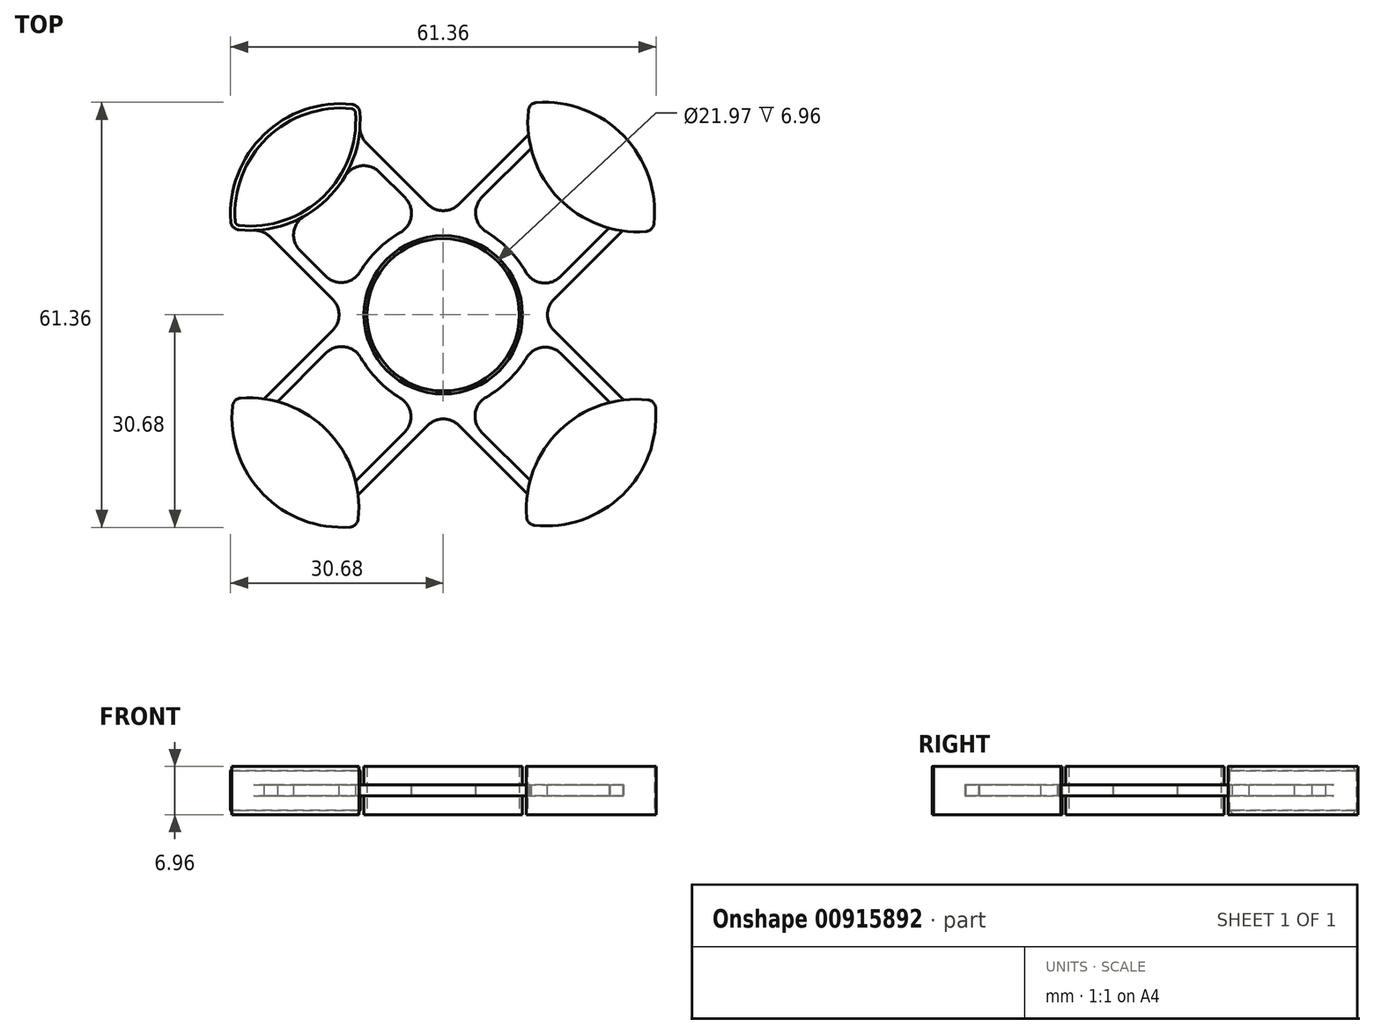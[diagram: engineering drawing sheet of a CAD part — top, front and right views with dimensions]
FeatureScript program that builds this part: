
annotation { "Feature Type Name" : "Feature", "Feature Type Description" : "" }
export const myFeature = defineFeature(function(context is Context, id is Id, definition is map)
    precondition{}
    {
        {
            var Q0;
            Q0=qCreatedBy(makeId("Top.planeOp"),FACE);
            var sketch = newSketch(context, id + "F0", { "sketchPlane" : qUnion([Q0])});
            skCircle(sketch, "E0", {"center": v(0, 0) * mm, "radius": 11.43 * mm});
            skLineSegment(sketch, "E1", {"start": v(-28.3, 14.58) * mm, "end": v(-14.37, 28.08) * mm});
            skLineSegment(sketch, "E2.MirrorCS", {"start": v(-14.37, 28.08) * mm, "end": v(0, 13.72) * mm});
            skLineSegment(sketch, "E3.MirrorCS", {"start": v(-13.72, 0) * mm, "end": v(-28.3, 14.58) * mm});
            skLineSegment(sketch, "E4", {"start": v(-13.73, 2.35) * mm, "end": v(-24.41, 13.03) * mm});
            skLineSegment(sketch, "E5", {"start": v(-12.86, 24.24) * mm, "end": v(-2.17, 13.55) * mm});
            skArc(sketch, "E6", {"start": v(-2.17, 13.55) * mm, "mid": v(-9.4, 9.45) * mm, "end": v(-13.73, 2.35) * mm});
            skArc(sketch, "E7", {"start": v(-12.86, 24.24) * mm, "mid": v(-20.1, 20.14) * mm, "end": v(-24.41, 13.03) * mm});
            skArc(sketch, "E8.1.0", {"start": v(-24.24, -12.86) * mm, "mid": v(-20.14, -20.1) * mm, "end": v(-13.03, -24.41) * mm});
            skArc(sketch, "E8.1.1", {"start": v(-13.55, -2.17) * mm, "mid": v(-9.45, -9.4) * mm, "end": v(-2.35, -13.73) * mm});
            skLineSegment(sketch, "E8.1.2", {"start": v(-14.58, -28.3) * mm, "end": v(-28.08, -14.37) * mm});
            skLineSegment(sketch, "E8.1.3", {"start": v(-24.24, -12.86) * mm, "end": v(-13.55, -2.17) * mm});
            skLineSegment(sketch, "E8.1.4", {"start": v(0, -13.72) * mm, "end": v(-14.58, -28.3) * mm});
            skLineSegment(sketch, "E8.1.5", {"start": v(-2.35, -13.73) * mm, "end": v(-13.03, -24.41) * mm});
            skLineSegment(sketch, "E8.1.6", {"start": v(-28.08, -14.37) * mm, "end": v(-13.72, 0) * mm});
            skArc(sketch, "E8.2.0", {"start": v(12.86, -24.24) * mm, "mid": v(20.1, -20.14) * mm, "end": v(24.41, -13.03) * mm});
            skArc(sketch, "E8.2.1", {"start": v(2.17, -13.55) * mm, "mid": v(9.4, -9.45) * mm, "end": v(13.73, -2.35) * mm});
            skLineSegment(sketch, "E8.2.2", {"start": v(28.3, -14.58) * mm, "end": v(14.37, -28.08) * mm});
            skLineSegment(sketch, "E8.2.3", {"start": v(12.86, -24.24) * mm, "end": v(2.17, -13.55) * mm});
            skLineSegment(sketch, "E8.2.4", {"start": v(13.72, 0) * mm, "end": v(28.3, -14.58) * mm});
            skLineSegment(sketch, "E8.2.5", {"start": v(13.73, -2.35) * mm, "end": v(24.41, -13.03) * mm});
            skLineSegment(sketch, "E8.2.6", {"start": v(14.37, -28.08) * mm, "end": v(0, -13.72) * mm});
            skArc(sketch, "E8.3.0", {"start": v(24.24, 12.86) * mm, "mid": v(20.14, 20.1) * mm, "end": v(13.03, 24.41) * mm});
            skArc(sketch, "E8.3.1", {"start": v(13.55, 2.17) * mm, "mid": v(9.45, 9.4) * mm, "end": v(2.35, 13.73) * mm});
            skLineSegment(sketch, "E8.3.2", {"start": v(14.58, 28.3) * mm, "end": v(28.08, 14.37) * mm});
            skLineSegment(sketch, "E8.3.3", {"start": v(24.24, 12.86) * mm, "end": v(13.55, 2.17) * mm});
            skLineSegment(sketch, "E8.3.4", {"start": v(0, 13.72) * mm, "end": v(14.58, 28.3) * mm});
            skLineSegment(sketch, "E8.3.5", {"start": v(2.35, 13.73) * mm, "end": v(13.03, 24.41) * mm});
            skLineSegment(sketch, "E8.3.6", {"start": v(28.08, 14.37) * mm, "end": v(13.72, 0) * mm});
            skSolve(sketch);
        }
        {
            var Q0;
            Q0=qSketchRegion(id+"F0",true);
            extrude(context, id + "F1", {"entities" : qUnion([Q0]), "endBound" : BoundingType.SYMMETRIC, "depth" : 1.59 * mm, "offsetDistance" : 25.4 * mm});
        }
        {
            var Q0;
            Q0=qCreatedBy(makeId("Top.planeOp"),FACE);
            var sketch = newSketch(context, id + "F2", { "sketchPlane" : qUnion([Q0])});
            skCircle(sketch, "E9", {"center": v(0, 0) * mm, "radius": 10.99 * mm});
            skCircle(sketch, "E10", {"center": v(0, 0) * mm, "radius": 11.43 * mm});
            skSolve(sketch);
        }
        {
            var Q0;
            Q0=qSketchRegion(id+"F2",true);
            extrude(context, id + "F3", {"entities" : qUnion([Q0]), "operationType" : NewBodyOperationType.ADD, "endBound" : BoundingType.SYMMETRIC, "depth" : 6.96 * mm, "offsetDistance" : 25.4 * mm});
        }
        {
            var Q0;
            Q0=qCreatedBy(makeId("Top.planeOp"),FACE);
            var sketch = newSketch(context, id + "F4", { "sketchPlane" : qUnion([Q0])});
            skArc(sketch, "E11.1.0", {"start": v(-30.64, 13.44) * mm, "mid": v(-25.86, 26) * mm, "end": v(-13.16, 30.4) * mm});
            skPoint(sketch, "E11.1.1", {"position": v(-30.53, 12.4) * mm});
            skArc(sketch, "E11.1.2", {"start": v(-29.5, 12.27) * mm, "mid": v(-16.8, 16.66) * mm, "end": v(-12.03, 29.22) * mm});
            skLineSegment(sketch, "E11.1.3", {"start": v(-30.53, 12.4) * mm, "end": v(-12.13, 30.25) * mm});
            skPoint(sketch, "E11.1.4", {"position": v(-12.13, 30.25) * mm});
            skPoint(sketch, "E11.1.5", {"position": v(-30.53, 12.4) * mm});
            skArc(sketch, "E11.1.6", {"start": v(-12.03, 29.22) * mm, "mid": v(-12.38, 30.01) * mm, "end": v(-13.16, 30.4) * mm});
            skArc(sketch, "E11.1.7", {"start": v(-30.64, 13.44) * mm, "mid": v(-30.28, 12.65) * mm, "end": v(-29.5, 12.27) * mm});
            skPoint(sketch, "E11.center", {"position": v(0, 0) * mm});
            skArc(sketch, "E12.1.0", {"start": v(-13.44, -30.64) * mm, "mid": v(-26, -25.86) * mm, "end": v(-30.4, -13.16) * mm});
            skPoint(sketch, "E12.1.1", {"position": v(-12.4, -30.53) * mm});
            skLineSegment(sketch, "E12.1.2", {"start": v(-12.4, -30.53) * mm, "end": v(-30.25, -12.13) * mm});
            skPoint(sketch, "E12.1.3", {"position": v(-30.25, -12.13) * mm});
            skArc(sketch, "E12.1.4", {"start": v(-12.27, -29.5) * mm, "mid": v(-16.66, -16.8) * mm, "end": v(-29.22, -12.03) * mm});
            skPoint(sketch, "E12.1.5", {"position": v(-12.4, -30.53) * mm});
            skArc(sketch, "E12.1.6", {"start": v(-13.44, -30.64) * mm, "mid": v(-12.65, -30.28) * mm, "end": v(-12.27, -29.5) * mm});
            skArc(sketch, "E12.1.7", {"start": v(-29.22, -12.03) * mm, "mid": v(-30.01, -12.38) * mm, "end": v(-30.4, -13.16) * mm});
            skArc(sketch, "E12.2.0", {"start": v(30.64, -13.44) * mm, "mid": v(25.86, -26) * mm, "end": v(13.16, -30.4) * mm});
            skPoint(sketch, "E12.2.1", {"position": v(30.53, -12.4) * mm});
            skLineSegment(sketch, "E12.2.2", {"start": v(30.53, -12.4) * mm, "end": v(12.13, -30.25) * mm});
            skPoint(sketch, "E12.2.3", {"position": v(12.13, -30.25) * mm});
            skArc(sketch, "E12.2.4", {"start": v(29.5, -12.27) * mm, "mid": v(16.8, -16.66) * mm, "end": v(12.03, -29.22) * mm});
            skPoint(sketch, "E12.2.5", {"position": v(30.53, -12.4) * mm});
            skArc(sketch, "E12.2.6", {"start": v(30.64, -13.44) * mm, "mid": v(30.28, -12.65) * mm, "end": v(29.5, -12.27) * mm});
            skArc(sketch, "E12.2.7", {"start": v(12.03, -29.22) * mm, "mid": v(12.38, -30.01) * mm, "end": v(13.16, -30.4) * mm});
            skArc(sketch, "E12.3.0", {"start": v(13.44, 30.64) * mm, "mid": v(26, 25.86) * mm, "end": v(30.4, 13.16) * mm});
            skPoint(sketch, "E12.3.1", {"position": v(12.4, 30.53) * mm});
            skLineSegment(sketch, "E12.3.2", {"start": v(12.4, 30.53) * mm, "end": v(30.25, 12.13) * mm});
            skPoint(sketch, "E12.3.3", {"position": v(30.25, 12.13) * mm});
            skArc(sketch, "E12.3.4", {"start": v(12.27, 29.5) * mm, "mid": v(16.66, 16.8) * mm, "end": v(29.22, 12.03) * mm});
            skPoint(sketch, "E12.3.5", {"position": v(12.4, 30.53) * mm});
            skArc(sketch, "E12.3.6", {"start": v(13.44, 30.64) * mm, "mid": v(12.65, 30.28) * mm, "end": v(12.27, 29.5) * mm});
            skArc(sketch, "E12.3.7", {"start": v(29.22, 12.03) * mm, "mid": v(30.01, 12.38) * mm, "end": v(30.4, 13.16) * mm});
            skSolve(sketch);
        }
        {
            var Q0;
            Q0=qSketchRegion(id+"F4",true);
            extrude(context, id + "F5", {"entities" : qUnion([Q0]), "operationType" : NewBodyOperationType.ADD, "endBound" : BoundingType.SYMMETRIC, "depth" : 6.96 * mm, "offsetDistance" : 25.4 * mm});
        }
        {
            var Q0;
            Q0=makeQuery(id+"F5.boolean.opBoolean","INTERSECT",EDGE,{"derivedFrom":[makeQuery(id+"F1.opExtrude","SWEPT_FACE",FACE,{"disambiguationData":[OSD([sQuery(id+"F0.wireOp",EDGE,"E3.MirrorCS")])]}),makeQuery(id+"F5.opExtrude","SWEPT_FACE",FACE,{"disambiguationData":[OSD([sQuery(id+"F4.wireOp",EDGE,"E11.1.2")])]})]});
            var Q1;
            Q1=makeQuery(id+"F5.boolean.opBoolean","INTERSECT",EDGE,{"derivedFrom":[makeQuery(id+"F1.opExtrude","SWEPT_FACE",FACE,{"disambiguationData":[OSD([sQuery(id+"F0.wireOp",EDGE,"E5")])]}),makeQuery(id+"F5.opExtrude","SWEPT_FACE",FACE,{"disambiguationData":[OSD([sQuery(id+"F4.wireOp",EDGE,"E11.1.2")])]})]});
            var Q2;
            Q2=makeQuery(id+"F5.boolean.opBoolean","INTERSECT",EDGE,{"derivedFrom":[makeQuery(id+"F1.opExtrude","SWEPT_FACE",FACE,{"disambiguationData":[OSD([sQuery(id+"F0.wireOp",EDGE,"E4")])]}),makeQuery(id+"F5.opExtrude","SWEPT_FACE",FACE,{"disambiguationData":[OSD([sQuery(id+"F4.wireOp",EDGE,"E11.1.2")])]})]});
            var Q3;
            Q3=makeQuery(id+"F5.boolean.opBoolean","INTERSECT",EDGE,{"derivedFrom":[makeQuery(id+"F1.opExtrude","SWEPT_FACE",FACE,{"disambiguationData":[OSD([sQuery(id+"F0.wireOp",EDGE,"E2.MirrorCS")])]}),makeQuery(id+"F5.opExtrude","SWEPT_FACE",FACE,{"disambiguationData":[OSD([sQuery(id+"F4.wireOp",EDGE,"E11.1.2")])]})]});
            var Q4;
            Q4=makeQuery(id+"F1.opExtrude","SWEPT_EDGE",EDGE,{"disambiguationData":[OSD([sQuery(id+"F0.wireOp",EDGE,"E5"),sQuery(id+"F0.wireOp",EDGE,"E6")])]});
            var Q5;
            Q5=makeQuery(id+"F1.opExtrude","SWEPT_EDGE",EDGE,{"disambiguationData":[OSD([sQuery(id+"F0.wireOp",EDGE,"E4"),sQuery(id+"F0.wireOp",EDGE,"E6")])]});
            var Q6;
            Q6=makeQuery(id+"F1.opExtrude","SWEPT_EDGE",EDGE,{"disambiguationData":[OSD([sQuery(id+"F0.wireOp",EDGE,"E3.MirrorCS"),sQuery(id+"F0.wireOp",EDGE,"E8.1.6")])]});
            var Q7;
            Q7=makeQuery(id+"F1.opExtrude","SWEPT_EDGE",EDGE,{"disambiguationData":[OSD([sQuery(id+"F0.wireOp",EDGE,"E2.MirrorCS"),sQuery(id+"F0.wireOp",EDGE,"E8.3.4")])]});
            var Q8;
            Q8=makeQuery(id+"F5.boolean.opBoolean","INTERSECT",EDGE,{"derivedFrom":[makeQuery(id+"F1.opExtrude","SWEPT_FACE",FACE,{"disambiguationData":[OSD([sQuery(id+"F0.wireOp",EDGE,"E8.3.6")])]}),makeQuery(id+"F5.opExtrude","SWEPT_FACE",FACE,{"disambiguationData":[OSD([sQuery(id+"F4.wireOp",EDGE,"2GfptWYo-hmfW-X0eh-p7IZ-oyEZ6vwRamwt")])]})]});
            var Q9;
            Q9=makeQuery(id+"F5.boolean.opBoolean","INTERSECT",EDGE,{"derivedFrom":[makeQuery(id+"F1.opExtrude","SWEPT_FACE",FACE,{"disambiguationData":[OSD([sQuery(id+"F0.wireOp",EDGE,"E8.3.5")])]}),makeQuery(id+"F5.opExtrude","SWEPT_FACE",FACE,{"disambiguationData":[OSD([sQuery(id+"F4.wireOp",EDGE,"2GfptWYo-hmfW-X0eh-p7IZ-oyEZ6vwRamwt")])]})]});
            var Q10;
            Q10=makeQuery(id+"F5.boolean.opBoolean","INTERSECT",EDGE,{"derivedFrom":[makeQuery(id+"F1.opExtrude","SWEPT_FACE",FACE,{"disambiguationData":[OSD([sQuery(id+"F0.wireOp",EDGE,"E8.3.3")])]}),makeQuery(id+"F5.opExtrude","SWEPT_FACE",FACE,{"disambiguationData":[OSD([sQuery(id+"F4.wireOp",EDGE,"2GfptWYo-hmfW-X0eh-p7IZ-oyEZ6vwRamwt")])]})]});
            var Q11;
            Q11=makeQuery(id+"F5.boolean.opBoolean","INTERSECT",EDGE,{"derivedFrom":[makeQuery(id+"F1.opExtrude","SWEPT_FACE",FACE,{"disambiguationData":[OSD([sQuery(id+"F0.wireOp",EDGE,"E8.3.4")])]}),makeQuery(id+"F5.opExtrude","SWEPT_FACE",FACE,{"disambiguationData":[OSD([sQuery(id+"F4.wireOp",EDGE,"2GfptWYo-hmfW-X0eh-p7IZ-oyEZ6vwRamwt")])]})]});
            var Q12;
            Q12=makeQuery(id+"F1.opExtrude","SWEPT_EDGE",EDGE,{"disambiguationData":[OSD([sQuery(id+"F0.wireOp",EDGE,"E8.3.1"),sQuery(id+"F0.wireOp",EDGE,"E8.3.5")])]});
            var Q13;
            Q13=makeQuery(id+"F1.opExtrude","SWEPT_EDGE",EDGE,{"disambiguationData":[OSD([sQuery(id+"F0.wireOp",EDGE,"E8.3.1"),sQuery(id+"F0.wireOp",EDGE,"E8.3.3")])]});
            var Q14;
            Q14=makeQuery(id+"F1.opExtrude","SWEPT_EDGE",EDGE,{"disambiguationData":[OSD([sQuery(id+"F0.wireOp",EDGE,"E8.2.4"),sQuery(id+"F0.wireOp",EDGE,"E8.3.6")])]});
            var Q15;
            Q15=makeQuery(id+"F1.opExtrude","SWEPT_EDGE",EDGE,{"disambiguationData":[OSD([sQuery(id+"F0.wireOp",EDGE,"E8.2.1"),sQuery(id+"F0.wireOp",EDGE,"E8.2.5")])]});
            var Q16;
            Q16=makeQuery(id+"F1.opExtrude","SWEPT_EDGE",EDGE,{"disambiguationData":[OSD([sQuery(id+"F0.wireOp",EDGE,"E8.2.1"),sQuery(id+"F0.wireOp",EDGE,"E8.2.3")])]});
            var Q17;
            Q17=makeQuery(id+"F1.opExtrude","SWEPT_EDGE",EDGE,{"disambiguationData":[OSD([sQuery(id+"F0.wireOp",EDGE,"E8.1.4"),sQuery(id+"F0.wireOp",EDGE,"E8.2.6")])]});
            var Q18;
            Q18=makeQuery(id+"F1.opExtrude","SWEPT_EDGE",EDGE,{"disambiguationData":[OSD([sQuery(id+"F0.wireOp",EDGE,"E8.1.1"),sQuery(id+"F0.wireOp",EDGE,"E8.1.5")])]});
            var Q19;
            Q19=makeQuery(id+"F1.opExtrude","SWEPT_EDGE",EDGE,{"disambiguationData":[OSD([sQuery(id+"F0.wireOp",EDGE,"E8.1.1"),sQuery(id+"F0.wireOp",EDGE,"E8.1.3")])]});
            var Q20;
            Q20=makeQuery(id+"F5.boolean.opBoolean","INTERSECT",EDGE,{"derivedFrom":[makeQuery(id+"F1.opExtrude","SWEPT_FACE",FACE,{"disambiguationData":[OSD([sQuery(id+"F0.wireOp",EDGE,"E8.1.3")])]}),makeQuery(id+"F5.opExtrude","SWEPT_FACE",FACE,{"disambiguationData":[OSD([sQuery(id+"F4.wireOp",EDGE,"E11.2.2")])]})]});
            var Q21;
            Q21=makeQuery(id+"F5.boolean.opBoolean","INTERSECT",EDGE,{"derivedFrom":[makeQuery(id+"F1.opExtrude","SWEPT_FACE",FACE,{"disambiguationData":[OSD([sQuery(id+"F0.wireOp",EDGE,"E8.1.5")])]}),makeQuery(id+"F5.opExtrude","SWEPT_FACE",FACE,{"disambiguationData":[OSD([sQuery(id+"F4.wireOp",EDGE,"E11.2.2")])]})]});
            var Q22;
            Q22=makeQuery(id+"F5.boolean.opBoolean","INTERSECT",EDGE,{"derivedFrom":[makeQuery(id+"F1.opExtrude","SWEPT_FACE",FACE,{"disambiguationData":[OSD([sQuery(id+"F0.wireOp",EDGE,"E8.2.3")])]}),makeQuery(id+"F5.opExtrude","SWEPT_FACE",FACE,{"disambiguationData":[OSD([sQuery(id+"F4.wireOp",EDGE,"E11.3.2")])]})]});
            var Q23;
            Q23=makeQuery(id+"F5.boolean.opBoolean","INTERSECT",EDGE,{"derivedFrom":[makeQuery(id+"F1.opExtrude","SWEPT_FACE",FACE,{"disambiguationData":[OSD([sQuery(id+"F0.wireOp",EDGE,"E8.2.5")])]}),makeQuery(id+"F5.opExtrude","SWEPT_FACE",FACE,{"disambiguationData":[OSD([sQuery(id+"F4.wireOp",EDGE,"E11.3.2")])]})]});
            var Q24;
            Q24=makeQuery(id+"F5.boolean.opBoolean","INTERSECT",EDGE,{"derivedFrom":[makeQuery(id+"F1.opExtrude","SWEPT_FACE",FACE,{"disambiguationData":[OSD([sQuery(id+"F0.wireOp",EDGE,"E8.2.4")])]}),makeQuery(id+"F5.opExtrude","SWEPT_FACE",FACE,{"disambiguationData":[OSD([sQuery(id+"F4.wireOp",EDGE,"E11.3.2")])]})]});
            var Q25;
            Q25=makeQuery(id+"F5.boolean.opBoolean","INTERSECT",EDGE,{"derivedFrom":[makeQuery(id+"F1.opExtrude","SWEPT_FACE",FACE,{"disambiguationData":[OSD([sQuery(id+"F0.wireOp",EDGE,"E8.2.6")])]}),makeQuery(id+"F5.opExtrude","SWEPT_FACE",FACE,{"disambiguationData":[OSD([sQuery(id+"F4.wireOp",EDGE,"E11.3.2")])]})]});
            var Q26;
            Q26=makeQuery(id+"F5.boolean.opBoolean","INTERSECT",EDGE,{"derivedFrom":[makeQuery(id+"F1.opExtrude","SWEPT_FACE",FACE,{"disambiguationData":[OSD([sQuery(id+"F0.wireOp",EDGE,"E8.1.4")])]}),makeQuery(id+"F5.opExtrude","SWEPT_FACE",FACE,{"disambiguationData":[OSD([sQuery(id+"F4.wireOp",EDGE,"E11.2.2")])]})]});
            var Q27;
            Q27=makeQuery(id+"F5.boolean.opBoolean","INTERSECT",EDGE,{"derivedFrom":[makeQuery(id+"F1.opExtrude","SWEPT_FACE",FACE,{"disambiguationData":[OSD([sQuery(id+"F0.wireOp",EDGE,"E8.1.6")])]}),makeQuery(id+"F5.opExtrude","SWEPT_FACE",FACE,{"disambiguationData":[OSD([sQuery(id+"F4.wireOp",EDGE,"E11.2.2")])]})]});
            fillet(context, id + "F6", {"entities" : qUnion([Q0, Q1, Q2, Q3, Q4, Q5, Q6, Q7, Q8, Q9, Q10, Q11, Q12, Q13, Q14, Q15, Q16, Q17, Q18, Q19, Q20, Q21, Q22, Q23, Q24, Q25, Q26, Q27]), "radius" : 3.17 * mm, "tangentPropagation" : true, "allowEdgeOverflow" : false});
        }
        {
            var Q0;
            Q0=makeQuery(id+"F5.opExtrude","CAP_FACE",FACE,{"disambiguationData":[OSD([sQuery(id+"F4.wireOp",EDGE,"E11.1.0"),sQuery(id+"F4.wireOp",EDGE,"E11.1.2"),sQuery(id+"F4.wireOp",EDGE,"E11.1.6"),sQuery(id+"F4.wireOp",EDGE,"E11.1.7")])],"isStart":false});
            var Q1;
            Q1=makeQuery(id+"F5.opExtrude","CAP_FACE",FACE,{"disambiguationData":[OSD([sQuery(id+"F4.wireOp",EDGE,"E11.2.0"),sQuery(id+"F4.wireOp",EDGE,"E11.2.2"),sQuery(id+"F4.wireOp",EDGE,"E11.2.6"),sQuery(id+"F4.wireOp",EDGE,"E11.2.7")])],"isStart":false});
            var Q2;
            Q2=makeQuery(id+"F5.opExtrude","CAP_FACE",FACE,{"disambiguationData":[OSD([sQuery(id+"F4.wireOp",EDGE,"E11.3.0"),sQuery(id+"F4.wireOp",EDGE,"E11.3.2"),sQuery(id+"F4.wireOp",EDGE,"E11.3.6"),sQuery(id+"F4.wireOp",EDGE,"E11.3.7")])],"isStart":false});
            var Q3;
            Q3=makeQuery(id+"F5.opExtrude","CAP_FACE",FACE,{"disambiguationData":[OSD([sQuery(id+"F4.wireOp",EDGE,"2GfptWYo-hmfW-X0eh-p7IZ-oyEZ6vwRamwt"),sQuery(id+"F4.wireOp",EDGE,"800a4ff0-f1a6-4ab4-8c3e-908917e631de0.MirrorCS"),sQuery(id+"F4.wireOp",EDGE,"d74e7ebc-f6b9-43e4-8dfe-54d4acb7e41b.filletArc"),sQuery(id+"F4.wireOp",EDGE,"0e665434-a23b-4a2b-bd05-1e0ce9fd26f7.filletArc")])],"isStart":false});
            var Q4;
            Q4=makeQuery(id+"F5.opExtrude","CAP_FACE",FACE,{"disambiguationData":[OSD([sQuery(id+"F4.wireOp",EDGE,"E11.1.0"),sQuery(id+"F4.wireOp",EDGE,"E11.1.2"),sQuery(id+"F4.wireOp",EDGE,"E11.1.6"),sQuery(id+"F4.wireOp",EDGE,"E11.1.7")])],"isStart":true});
            var Q5;
            Q5=makeQuery(id+"F5.opExtrude","CAP_FACE",FACE,{"disambiguationData":[OSD([sQuery(id+"F4.wireOp",EDGE,"E11.3.0"),sQuery(id+"F4.wireOp",EDGE,"E11.3.2"),sQuery(id+"F4.wireOp",EDGE,"E11.3.6"),sQuery(id+"F4.wireOp",EDGE,"E11.3.7")])],"isStart":true});
            var Q6;
            Q6=makeQuery(id+"F5.opExtrude","CAP_FACE",FACE,{"disambiguationData":[OSD([sQuery(id+"F4.wireOp",EDGE,"2GfptWYo-hmfW-X0eh-p7IZ-oyEZ6vwRamwt"),sQuery(id+"F4.wireOp",EDGE,"800a4ff0-f1a6-4ab4-8c3e-908917e631de0.MirrorCS"),sQuery(id+"F4.wireOp",EDGE,"d74e7ebc-f6b9-43e4-8dfe-54d4acb7e41b.filletArc"),sQuery(id+"F4.wireOp",EDGE,"0e665434-a23b-4a2b-bd05-1e0ce9fd26f7.filletArc")])],"isStart":true});
            var Q7;
            Q7=makeQuery(id+"F5.opExtrude","CAP_FACE",FACE,{"disambiguationData":[OSD([sQuery(id+"F4.wireOp",EDGE,"E11.2.0"),sQuery(id+"F4.wireOp",EDGE,"E11.2.2"),sQuery(id+"F4.wireOp",EDGE,"E11.2.6"),sQuery(id+"F4.wireOp",EDGE,"E11.2.7")])],"isStart":true});
            chamfer(context, id + "F7", {"entities" : qUnion([Q0, Q1, Q2, Q3, Q4, Q5, Q6, Q7]), "width" : 0.64 * mm, "tangentPropagation" : true});
        }
    });
